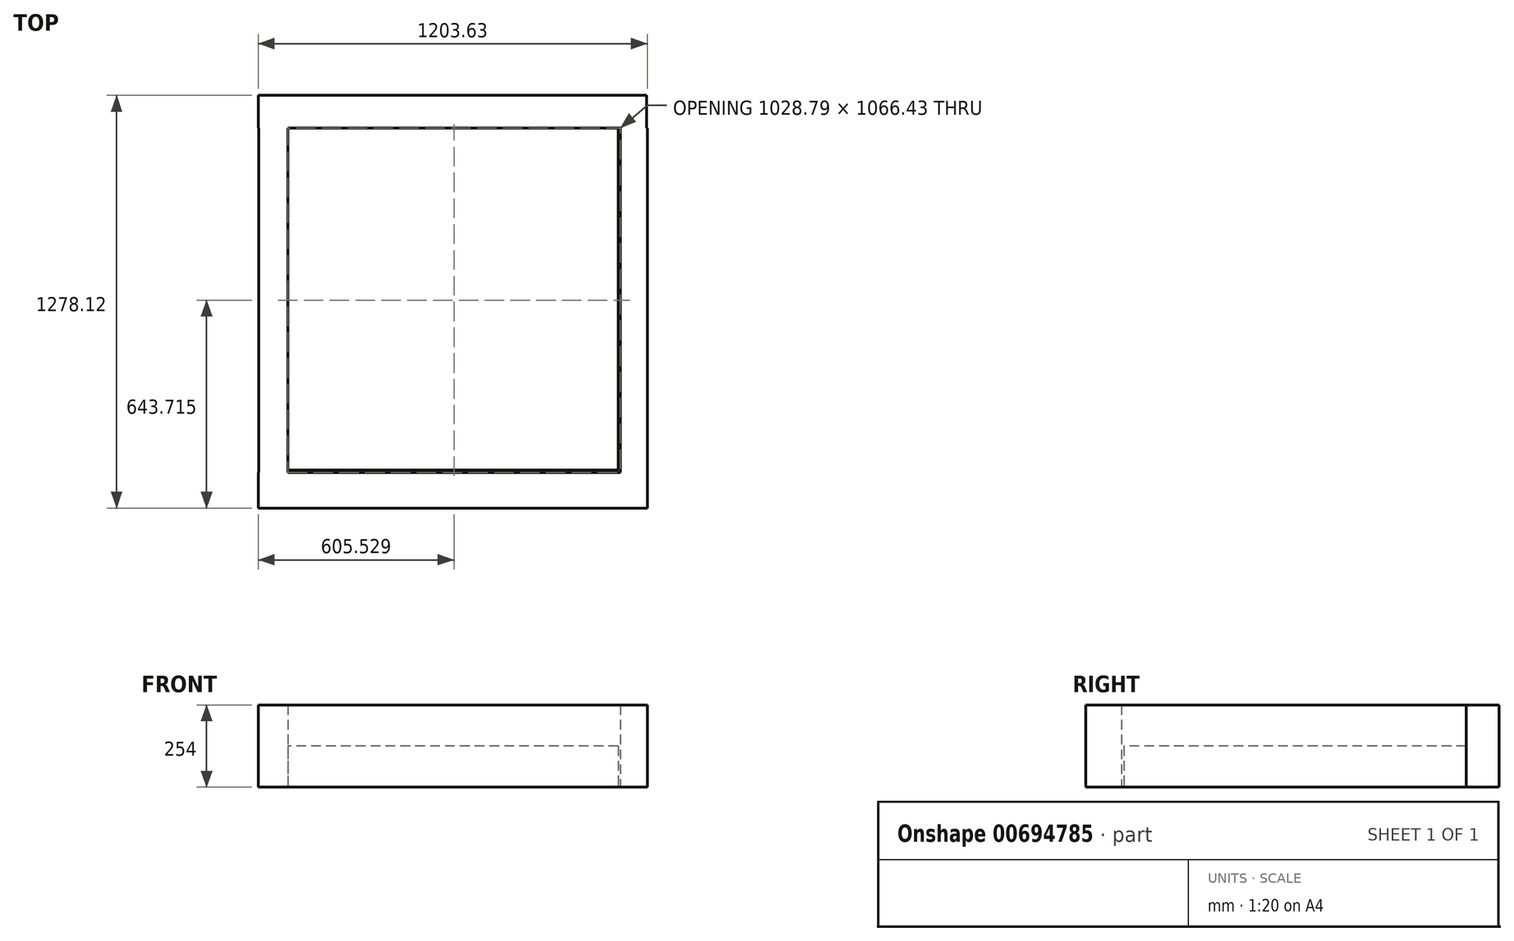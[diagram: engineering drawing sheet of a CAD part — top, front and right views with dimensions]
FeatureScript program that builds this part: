
annotation { "Feature Type Name" : "Feature", "Feature Type Description" : "" }
export const myFeature = defineFeature(function(context is Context, id is Id, definition is map)
    precondition{}
    {
        {
            var Q0;
            Q0=qCreatedBy(makeId("Top.planeOp"),FACE);
            var sketch = newSketch(context, id + "F0", { "sketchPlane" : qUnion([Q0])});
            skLineSegment(sketch, "E0.bottom", {"start": v(511.83, 529.68) * mm, "end": v(-511.83, 529.68) * mm});
            skLineSegment(sketch, "E0.top", {"start": v(511.83, -529.68) * mm, "end": v(-511.83, -529.68) * mm});
            skLineSegment(sketch, "E0.left", {"start": v(511.83, 529.68) * mm, "end": v(511.83, -529.68) * mm});
            skLineSegment(sketch, "E0.right", {"start": v(-511.83, 529.68) * mm, "end": v(-511.83, -529.68) * mm});
            skPoint(sketch, "E0.middle", {"position": v(0, 0) * mm});
            skSolve(sketch);
        }
        {
            var Q0;
            Q0=makeQuery(id+"F0.imprint","IMPRINT",FACE,{"disambiguationData":[TD([[makeQuery(id+"F0.imprint","IMPRINT",EDGE,{"derivedFrom":sQuery(id+"F0.wireOp",EDGE,"E0.bottom")}),1.0]])]});
            var sketch = newSketch(context, id + "F1", { "sketchPlane" : qUnion([Q0])});
            skLineSegment(sketch, "E1.bottom", {"start": v(-602, -536.5) * mm, "end": v(601.64, -536.5) * mm});
            skLineSegment(sketch, "E1.top", {"start": v(-602, -647) * mm, "end": v(601.64, -647) * mm});
            skLineSegment(sketch, "E1.left", {"start": v(-602, -536.5) * mm, "end": v(-602, -647) * mm});
            skLineSegment(sketch, "E1.right", {"start": v(601.64, -536.5) * mm, "end": v(601.64, -647) * mm});
            skLineSegment(sketch, "E2.bottom", {"start": v(-601.39, 529.92) * mm, "end": v(600.14, 529.92) * mm});
            skLineSegment(sketch, "E2.top", {"start": v(-601.39, 631.11) * mm, "end": v(600.14, 631.11) * mm});
            skLineSegment(sketch, "E2.left", {"start": v(-601.39, 529.92) * mm, "end": v(-601.39, 631.11) * mm});
            skLineSegment(sketch, "E2.right", {"start": v(600.14, 529.92) * mm, "end": v(600.14, 631.11) * mm});
            skLineSegment(sketch, "E3.bottom", {"start": v(601.64, -536.5) * mm, "end": v(517.93, -536.5) * mm});
            skLineSegment(sketch, "E3.top", {"start": v(601.64, 529.92) * mm, "end": v(517.93, 529.92) * mm});
            skLineSegment(sketch, "E3.left", {"start": v(601.64, -536.5) * mm, "end": v(601.64, 529.92) * mm});
            skLineSegment(sketch, "E3.right", {"start": v(517.93, -536.5) * mm, "end": v(517.93, 529.92) * mm});
            skLineSegment(sketch, "E4.bottom", {"start": v(-510.86, -536.5) * mm, "end": v(-600.31, -536.5) * mm});
            skLineSegment(sketch, "E4.top", {"start": v(-510.86, 529.92) * mm, "end": v(-600.31, 529.92) * mm});
            skLineSegment(sketch, "E4.left", {"start": v(-510.86, -536.5) * mm, "end": v(-510.86, 529.92) * mm});
            skLineSegment(sketch, "E4.right", {"start": v(-600.31, -536.5) * mm, "end": v(-600.31, 529.92) * mm});
            skSolve(sketch);
        }
        {
            var Q0;
            Q0 = qSketchRegion(id + "F0", true);
            extrude(context, id + "F2", {"entities" : qUnion([Q0]), "depth" : 127 * mm, "offsetDistance" : 25.4 * mm});
        }
        {
            var Q0;
            Q0 = qSketchRegion(id + "F1", true);
            extrude(context, id + "F3", {"entities" : qUnion([Q0]), "operationType" : NewBodyOperationType.ADD, "depth" : 254 * mm, "offsetDistance" : 25.4 * mm});
        }
    });
